# Revit family: Shower-Handshower_Kit-KOHLER-Aleo-K-72282K_1
name_source: partatom
category: Plumbing Fixtures
units: mm (PartAtom-declared; Revit-internal decimal feet)

## family parameters
Cut with Voids When Loaded = No
Host = Face
OmniClass Number = 23.31.17.00
OmniClass Title = Showers
Part Type = Normal
Room Calculation Point = No
Round Connector Dimension = Use Diameter
Shared = No

## types (2) — shared parameters
ADA Compliant = No
Assembly Code = D2010700
CW Connection = Yes
Cold Water Inlet = Cold Water Inlet
Date Modified = 11/24/2022
Description = Wall Mount Bath Shower Faucet
Drain Included = No
Flow Rate = 4 GPM
HW Connection = Yes
Handle Clearance = 3 5/8"
Handshower Flow Rate = 2 GPM
Handshower Pressure = 80.00 psi
Height = 18 5/8"
Hot Water Inlet = Hot Water Inlet
Length = 9 13/16"
Manufacturer = KOHLER Co.
Master Format 2014 = 22 42 23
Master Format 2014 Name = Residential Showers
Material = Premium Metal Construction
Pressure = 45.00 psi
Product Name = Aleo
Spout Reach = 4 7/16"
URL = https://www.kohlerasiapacific.com
Vent Connection = No
Waste Connection = No
Waste Water Outlet = Waste Water Outlet
WaterSense Certified = No
Width = 5 15/16"

## per-type parameters (varying)
| type | Default Elevation | Finish | Model | Secondary Finish | Tertiary Finish | Type |
| BL-Matte Black | 42" | Kohler-Metal-BL-Matte_Black | K-72282K-4-BL | Kohler-Plastic-2BL-Black | Kohler-Plastic-2BL-Black | 1 |
| CP-Polished Chrome | 0" | Kohler-Metal-CP-Polished_Chrome | K-72282K-4-CP | Kohler-Plastic-58-Thunder_Grey | Kohler-Plastic-0-White | 2 |

## geometry (parser evidence)
native form markers: Sweep x4
no freeform markers — native parametric forms only
